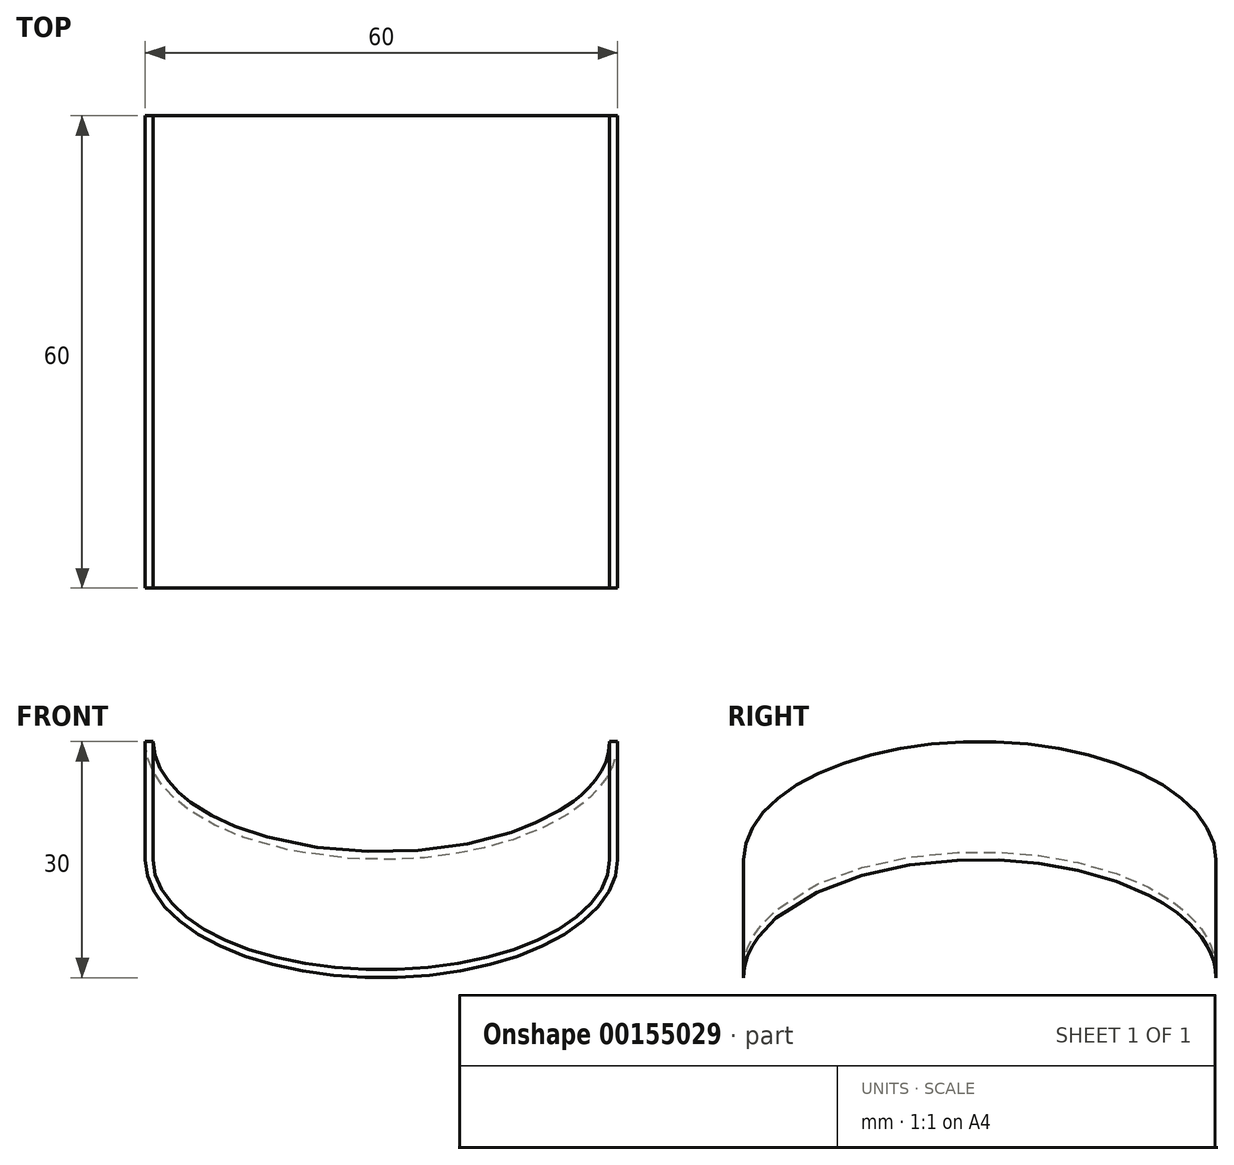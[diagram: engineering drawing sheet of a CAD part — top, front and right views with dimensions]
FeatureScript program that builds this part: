
annotation { "Feature Type Name" : "Feature", "Feature Type Description" : "" }
export const myFeature = defineFeature(function(context is Context, id is Id, definition is map)
    precondition{}
    {
        {
            var Q0;
            Q0=qCreatedBy(makeId("Front.planeOp"),FACE);
            var sketch = newSketch(context, id + "F0", { "sketchPlane" : qUnion([Q0])});
            skEllipticalArc(sketch, "E0", {});
            skEllipticalArc(sketch, "E1", {});
            skLineSegment(sketch, "E2", {"start": v(30, 15) * mm, "end": v(29, 15) * mm});
            skLineSegment(sketch, "E3", {"start": v(-29, 15) * mm, "end": v(-30, 15) * mm});
            const initialGuessF0  = {"E0": [0, 0.015, 1, 0, 0.03, 0.015, 3.141592653589793, 0], "E1": [0, 0.015, -1, 0, 0.029, 0.014, 0, 3.141592653589793]};
            skSetInitialGuess(sketch, initialGuessF0);
            skSolve(sketch);
        }
        {
            var Q0;
            Q0=qCreatedBy(makeId("Right.planeOp"),FACE);
            var sketch = newSketch(context, id + "F1", { "sketchPlane" : qUnion([Q0])});
            skEllipticalArc(sketch, "E4", {});
            const initialGuessF1  = {"E4": [0, -0.015, 1, 0, 0.03, 0.015, 0, 3.141592653589793]};
            skSetInitialGuess(sketch, initialGuessF1);
            skSolve(sketch);
        }
        {
            var Q0;
            Q0 = qSketchRegion(id + "F0", true);
            var Q1;
            Q1=sQuery(id+"F0.wireOp",EDGE,"f34d5eb2-35be-43cf-9de9-cc92b2d1d2182");
            var Q2;
            Q2 = qConstructionFilter(qBodyType(qCreatedBy(id + "F1" ,EDGE), BodyType.WIRE), ConstructionObject.NO);
            sweep(context, id + "F2", {"profiles" : qUnion([Q0]), "surfaceProfiles" : qUnion([Q1]), "path" : qUnion([Q2]), "keepProfileOrientation" : true});
        }
    });
